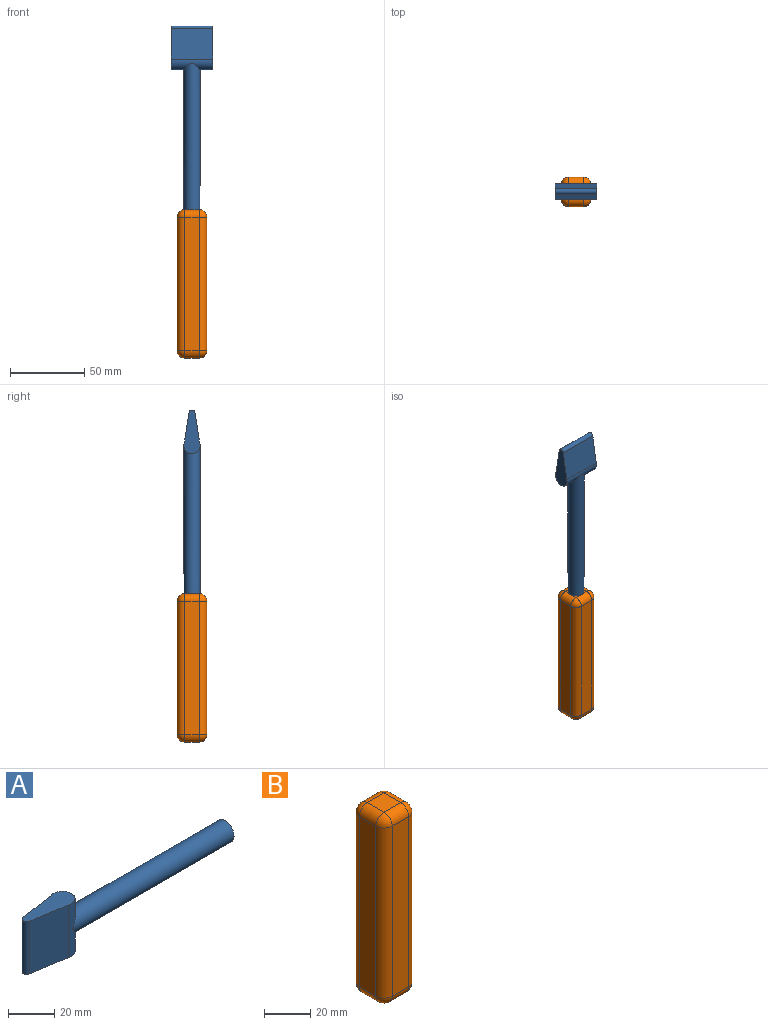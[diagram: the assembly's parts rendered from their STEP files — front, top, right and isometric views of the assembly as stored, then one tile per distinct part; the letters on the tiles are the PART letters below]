
ASSEMBLY  parts=2 mates=1
PART A: 8 faces, bbox 124x11x28 mm
  f0: cylinder r=5.5mm len=28mm, axis (0,0,-1), area 467mm2, adj f2,f3,f4,f5,f6
  f1: cylinder r=2mm len=28mm, axis (0,0,-1), area 158.4mm2, adj f2,f3,f4,f5
  f2: plane 28x20.62mm, normal (-0.16,-0.99,0), area 584.4mm2, adj f0,f1,f4,f5
  f3: plane 28x20.62mm, normal (-0.16,0.99,0), area 584.4mm2, adj f0,f1,f4,f5
  f4: plane 29.5x11mm, normal (0,0,1), area 219.5mm2, adj f0,f1,f2,f3
  f5: plane 29.5x11mm, normal (0,0,-1), area 219.5mm2, adj f0,f1,f2,f3
  f6: cylinder r=5.4mm len=98.97mm, axis (-1,0,0), area 3269.5mm2, adj f0,f7
  f7: plane 10.8x10.8mm, normal (1,0,0), area 91.7mm2, adj f6
PART B: 26 faces, bbox 20x20x100 mm
  f0: plane 90x10mm, normal (1,0,0), area 900mm2, adj f14,f19,f22,f25
  f1: plane 90x10mm, normal (0,1,0), area 900mm2, adj f11,f20,f21,f25
  f2: plane 90x10mm, normal (-1,0,0), area 900mm2, adj f6,f10,f11,f12
  f3: plane 90x10mm, normal (0,-1,0), area 900mm2, adj f6,f9,f13,f14
  f4: plane 10x10mm, normal (0,0,1), area 100mm2, adj f9,f10,f19,f20
  f5: plane 10x10mm, normal (0,0,-1), area 100mm2, adj f12,f13,f21,f22
  f6: cylinder r=5mm len=90mm, axis (0,0,-1), area 706.9mm2, adj f2,f3,f7,f8
  f7: sphere r=5mm, area 39.3mm2, adj f6,f9,f10
  f8: sphere r=5mm, area 39.3mm2, adj f6,f12,f13
  f9: cylinder r=5mm len=10mm, axis (-1,0,0), area 78.5mm2, adj f3,f4,f7,f15
  f10: cylinder r=5mm len=10mm, axis (0,1,0), area 78.5mm2, adj f2,f4,f7,f16
  f11: cylinder r=5mm len=90mm, axis (0,0,1), area 706.9mm2, adj f1,f2,f16,f17
  f12: cylinder r=5mm len=10mm, axis (0,-1,0), area 78.5mm2, adj f2,f5,f8,f17
  f13: cylinder r=5mm len=10mm, axis (1,0,0), area 78.5mm2, adj f3,f5,f8,f18
  f14: cylinder r=5mm len=90mm, axis (0,0,1), area 706.9mm2, adj f0,f3,f15,f18
  f15: sphere r=5mm, area 39.3mm2, adj f9,f14,f19
  f16: sphere r=5mm, area 39.3mm2, adj f10,f11,f20
  f17: sphere r=5mm, area 39.3mm2, adj f11,f12,f21
  f18: sphere r=5mm, area 39.3mm2, adj f13,f14,f22
  f19: cylinder r=5mm len=10mm, axis (0,-1,0), area 78.5mm2, adj f0,f4,f15,f23
  f20: cylinder r=5mm len=10mm, axis (1,0,0), area 78.5mm2, adj f1,f4,f16,f23
  f21: cylinder r=5mm len=10mm, axis (-1,0,0), area 78.5mm2, adj f1,f5,f17,f24
  f22: cylinder r=5mm len=10mm, axis (0,1,0), area 78.5mm2, adj f0,f5,f18,f24
  f23: sphere r=5mm, area 39.3mm2, adj f19,f20,f25
  f24: sphere r=5mm, area 39.3mm2, adj f21,f22,f25
  f25: cylinder r=5mm len=90mm, axis (0,0,-1), area 706.9mm2, adj f0,f1,f23,f24
PLACE A rot(axis=(0.71,0,-0.71),180deg) t=(126.26,-10.6,53.67)mm
PLACE B t=(164.33,-24.7,-146.33)mm
MATE cylindrical A.f6 <-> B.f4  axis (0,0,1) through (126.26,-10.6,-46.33)mm
